# Revit family: Strangregulierventil für Differenzdruckmessung, Geradsitzform 4218 GF
name_source: partatom
category: Rohrzubehör
revit_build: Autodesk Revit 2018 (Build: 20190510_1515(x64)
units: mm (PartAtom-declared; Revit-internal decimal feet)

## family parameters
Arbeitsebenenbasiert = Nein
Beim Laden mit Abzugskörper schneiden = Nein
Bemaßung runder Anschluss = Durchmesser verwenden
Gemeinsam genutzt = Nein
Immer vertikal = Ja
OmniClass-Nummer = 23.65.55.14
OmniClass-Titel = Valves for Liquid Services
Teiletyp = Unterbricht

## types (1)
- Strangregulierventil für Differenzdruckmessung, Geradsitzform 4218 GF
    Anwendungen = Zum hydraulischenAbgleich in Heiz- oder Kühlanlagen, Einregulieren und Absperren von Verteilleitungen, Strängen, Wärmetauschern, Heiz- und Kühlregistern.
    Ausführung = Geradsitzform, Gehäuse Grauguss GJL 250 nach EN 1561, Flansche nach EN 1092, PN 16, blau lackiert.
Ventiloberteil Grauguss GJL 250, mit nicht steigender Spindel, Spindelabdichtung durch Drei-fach-O-Ring.
Digitale Anzeige der Voreinstellstuffe.
    Differenzdruckmessnung = Das Strömax GF Strangregulierventil ist mit zwei Schnellmessventilen ausgestattet:
Bei Verwendung eines geeigneten Messgerätes kann der Differenzdruck gemessen und dadurch die jeweilige Durchflussmenge in Abhängigkeit der Einstellstufe ermittelt werden.
An den HERZ Messcomputern ist außerdem direkt die jeweilige Durchflussmenge ablesbar (siehe Gerätehandbuch).
Bei Verwendung von Frostschutzmittel ändert sich die Dichte des Medium, die bei Differenzdruckmessungen entsprechend zu berücksichtigen ist.
    GT = 10 mm  [stored 0.0328084 ft]
    Gehäuse = Grauguss GJL 250 nach EN 1561
    Hersteller = HERZ Armaturen Ges.m.b.H.
    Max. Betriebsdruck = 1600000.0 Pa
    Max. Betriebstemperatur = 110 °C
    Medium = Heizwasserqualität entsprechend ÖNORM H 5195 bzw. VDI Richtlinie 2035.
Ethylen und Propylenglykol können in einem Verhältnis von 25-50 vol. [%] gemischt werden.
    Min. Betriebstemperatur = -10 °C
    O-Ringe = EPDM
    Oberteil = Grauguss GJL 250 nach EN 1561
    Regulierspindel = Messing / Edelstahl
    SCRNCODE = 05;07;02
    SCRNSEQ = ARM;ARM_TYP="STRV";2
    Spindel (ab DN125) = Edelstahl
    Spindel (bis DN100) = Messing
    URL = www.herz-armaturen.at
    Ventilkegel = Grauguss GJL 250 nach EN 1561/ EPDM beschichtet
    W01 = 85.00°
    W02 = 60.00°
    Zählvorrichtung = Kunststoff

note: [stored X ft] marks values corroborated as IEEE doubles in the binary element streams (Revit-internal decimal feet)
